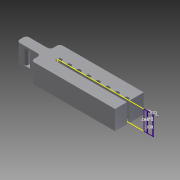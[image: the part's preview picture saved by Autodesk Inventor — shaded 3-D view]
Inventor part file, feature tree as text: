
AUTODESK INVENTOR PART (.ipt)
format: ipt  version: 2013 SP2 (Build 170200200, 200)  size: 264,192 bytes
history: native  units: in
note: dims shown in document units (in); Inventor stores cm internally (conversion verified against a paired STEP export)
features: sketch x10, extrude x9, fillet x3
ambient origin geometry x8: Origin, YZ Plane, XZ Plane, XY Plane, X Axis, Y Axis, Z Axis, Center Point
bodies: Solid1 (feature_tree)
feature tree (22):
  extrude  "Extrusion1"  Depth=0.16in
  extrude  "Extrusion2"  Depth=2.0in
  sketch  "Sketch3"  dims[d33=0.25in d34=0.0in d43=2.0in]
  extrude  "Extrusion4"  Depth=2.0in
  extrude  "Extrusion6"  Depth=0.14in
  extrude  "Extrusion7"  Depth=0.02in
  extrude  "Extrusion8"  Depth=0.14in
  extrude  "Extrusion9"  Depth=0.06in
  extrude  "Extrusion10"  Depth=0.06in
  extrude  "Extrusion11"  Depth=0.06in
  fillet  "Fillet7"  Radius=0.06in
  fillet  "Fillet8"  Radius=0.06in
  fillet  "Fillet9"  Radius=0.06in
  sketch  "Sketch1"  dims[d28=0.4693in d29=0.16in]
  sketch  "Sketch2"  dims[d30=0.4in d31=2.0in]
  sketch  "Sketch5"  dims[d69=0.049in d70=0.0in d71=0.14in]
  sketch  "Sketch9"  dims[d72=0.06in d73=0.02in]
  sketch  "Sketch10"  dims[d74=0.1in d78=0.14in]
  sketch  "Sketch11"  dims[d80=0.06in d82=0.06in]
  sketch  "Sketch12"  dims[d83=0.06in d84=0.06in]
  sketch  "Sketch13"  dims[d85=0.06in d86=0.06in d87=0.06in d88=0.06in d89=0.06in]
  sketch  "Sketch14"  dims[d90=0.06in d91=1.0in d92=0.0in d100=1.5in d102=0.25in d103=0.0in d104=0.25in d105=0.35in d106=0.0in d107=0.25in d108=1.5in d109=0.0in d110=1.5in d111=0.0in d112=0.2in d113=0.2in d114=0.5in d115=0.0in d116=0.2in d117=0.155in d118=0.155in d119=0.075in d120=0.5in d121=0.0in d122=0.0625in d123=0.0625in d124=0.0625in]
